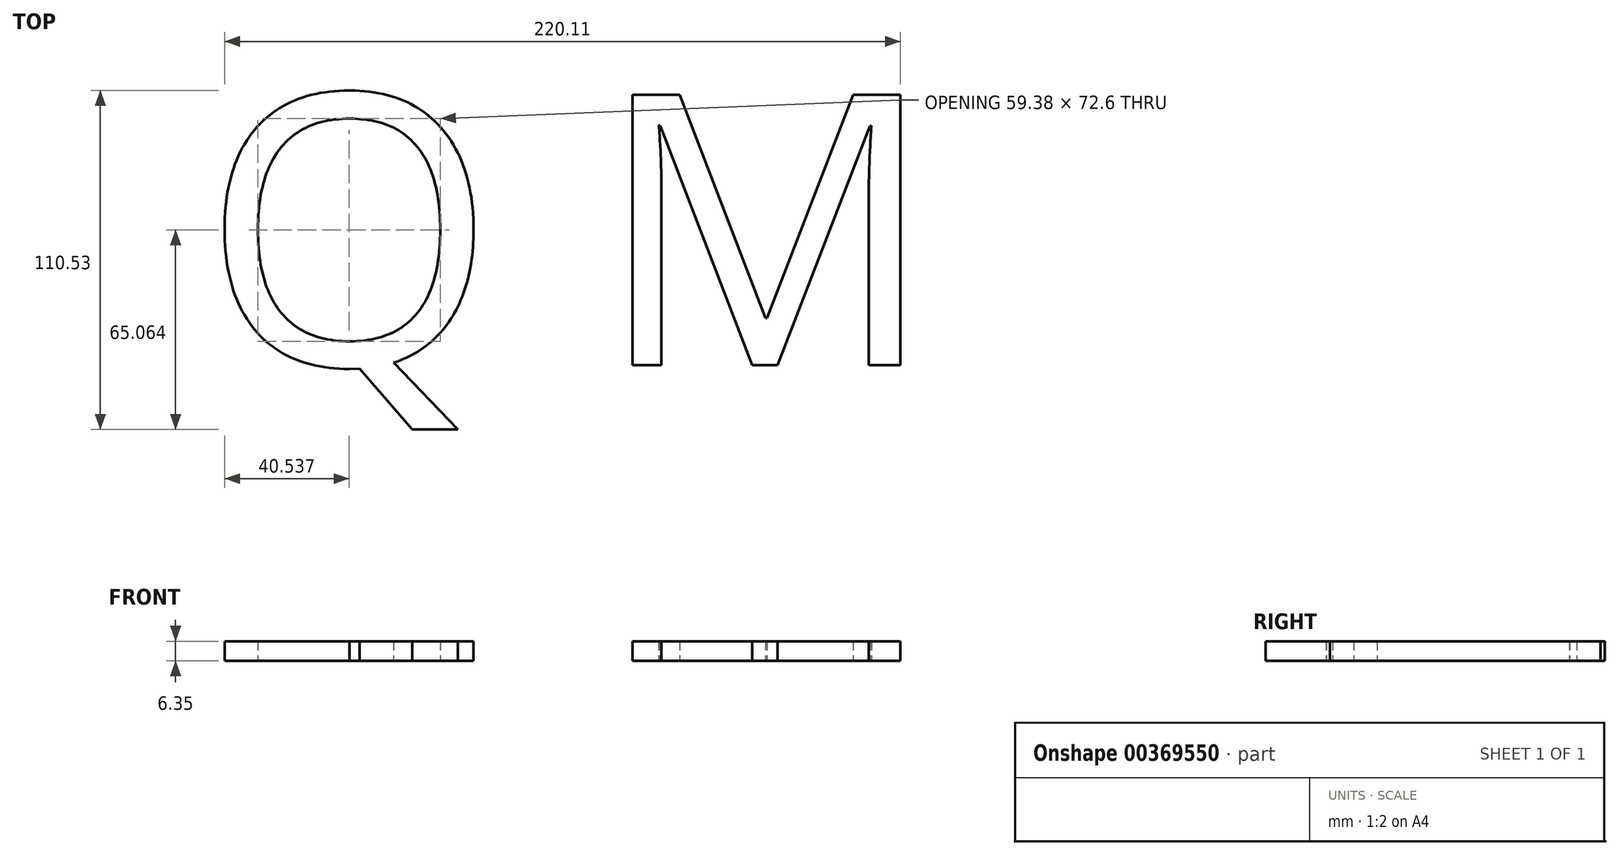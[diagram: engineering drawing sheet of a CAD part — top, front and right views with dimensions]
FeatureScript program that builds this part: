
annotation { "Feature Type Name" : "Feature", "Feature Type Description" : "" }
export const myFeature = defineFeature(function(context is Context, id is Id, definition is map)
    precondition{}
    {
        {
            var Q0;
            Q0=qCreatedBy(makeId("Top.planeOp"),FACE);
            var sketch = newSketch(context, id + "F0", { "sketchPlane" : qUnion([Q0])});
            skText(sketch, "E0", { "text": "Q M\n", "fontName": "OpenSans-Regular.ttf"});
            const initialGuessF0  = {"E0": [-0.07256, -0.05995, 1, 0, 0.0889]};
            skSetInitialGuess(sketch, initialGuessF0);
            skSolve(sketch);
        }
        {
            var Q0;
            Q0 = qSketchRegion(id + "F0", true);
            extrude(context, id + "F1", {"entities" : qUnion([Q0]), "depth" : 6.35 * mm});
        }
    });
